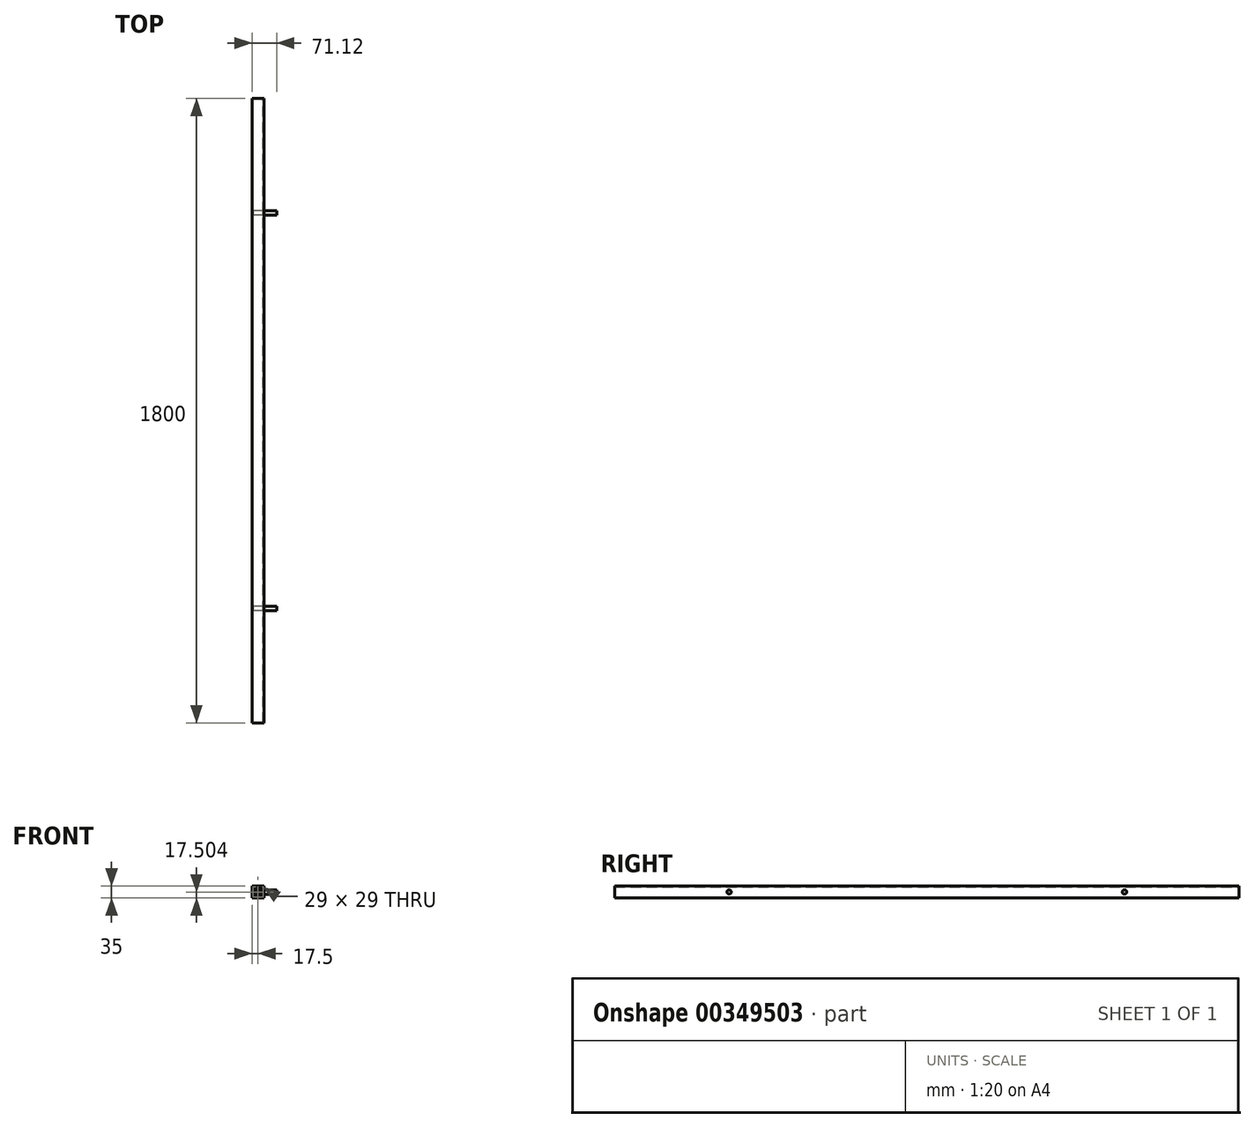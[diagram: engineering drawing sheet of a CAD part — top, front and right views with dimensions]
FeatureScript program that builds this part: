
annotation { "Feature Type Name" : "Feature", "Feature Type Description" : "" }
export const myFeature = defineFeature(function(context is Context, id is Id, definition is map)
    precondition{}
    {
        {
            var Q0;
            Q0=qCreatedBy(makeId("Front.planeOp"),FACE);
            var sketch = newSketch(context, id + "F0", { "sketchPlane" : qUnion([Q0])});
            skLineSegment(sketch, "E0.bottom", {"start": v(-235, 4.68) * mm, "end": v(-200, 4.68) * mm});
            skLineSegment(sketch, "E0.top", {"start": v(-235, -30.32) * mm, "end": v(-200, -30.32) * mm});
            skLineSegment(sketch, "E0.left", {"start": v(-235, 4.68) * mm, "end": v(-235, -30.32) * mm});
            skLineSegment(sketch, "E0.right", {"start": v(-200, 4.68) * mm, "end": v(-200, -30.32) * mm});
            skLineSegment(sketch, "E1.0", {"start": v(-232, -27.32) * mm, "end": v(-203, -27.32) * mm});
            skLineSegment(sketch, "E1.1", {"start": v(-232, 1.68) * mm, "end": v(-232, -27.32) * mm});
            skLineSegment(sketch, "E1.2", {"start": v(-232, 1.68) * mm, "end": v(-203, 1.68) * mm});
            skLineSegment(sketch, "E1.3", {"start": v(-203, 1.68) * mm, "end": v(-203, -27.32) * mm});
            skSolve(sketch);
        }
        {
            var Q0;
            Q0 = qSketchRegion(id + "F0", true);
            extrude(context, id + "F1", {"entities" : qUnion([Q0]), "depth" : 1800 * mm, "symmetric" : true});
        }
        {
            var Q0;
            Q0=makeQuery(id+"F1.opExtrude","SWEPT_FACE",FACE,{"disambiguationData":[OSD([sQuery(id+"F0.wireOp",EDGE,"E0.left")])]});
            var sketch = newSketch(context, id + "F2", { "sketchPlane" : qUnion([Q0])});
            skCircle(sketch, "E2", {"center": v(-569.98, -12.82) * mm, "radius": 6.25 * mm});
            skCircle(sketch, "E3.MirrorC", {"center": v(569.98, -12.82) * mm, "radius": 6.25 * mm});
            skSolve(sketch);
        }
        {
            var Q0;
            Q0 = qSketchRegion(id + "F2", true);
            extrude(context, id + "F3", {"entities" : qUnion([Q0]), "operationType" : NewBodyOperationType.ADD, "oppositeDirection" : true, "depth" : 71.12 * mm});
        }
    });
